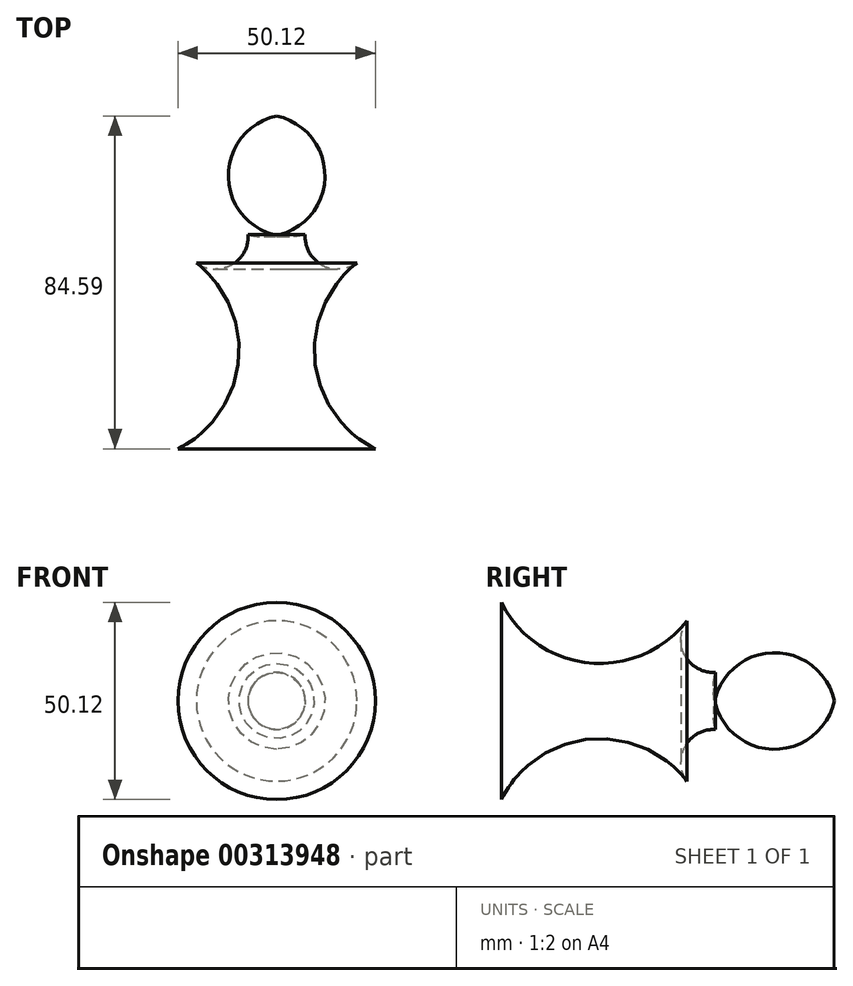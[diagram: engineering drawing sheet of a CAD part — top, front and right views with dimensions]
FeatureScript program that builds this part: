
annotation { "Feature Type Name" : "Feature", "Feature Type Description" : "" }
export const myFeature = defineFeature(function(context is Context, id is Id, definition is map)
    precondition{}
    {
        {
            var Q0;
            Q0=qCreatedBy(makeId("Top.planeOp"),FACE);
            var sketch = newSketch(context, id + "F0", { "sketchPlane" : qUnion([Q0])});
            skLineSegment(sketch, "E0", {"start": v(0, 44.58) * mm, "end": v(0, -40) * mm});
            skArc(sketch, "E1", {"start": v(0, 14.22) * mm, "mid": v(18.78, 29.4) * mm, "end": v(0, 44.58) * mm});
            skArc(sketch, "E2", {"start": v(7.25, 14.4) * mm, "mid": v(11.73, 6.55) * mm, "end": v(20.73, 7.47) * mm});
            skLineSegment(sketch, "E3", {"start": v(0, -40) * mm, "end": v(25.06, -40) * mm});
            skArc(sketch, "E4", {"start": v(20.73, 7.47) * mm, "mid": v(9.67, -17.48) * mm, "end": v(25.06, -40) * mm});
            skSolve(sketch);
        }
        {
            var Q0;
            {var subQ7=sQuery(id+"F0.wireOp",EDGE,"E3");Q0=makeQuery(id+"F0.imprint","IMPRINT",FACE,{"disambiguationData":[TD([[makeQuery(id+"F0.imprint","IMPRINT",EDGE,{"derivedFrom":subQ7}),1.0]])]});}
            var Q1;
            {var subQ0=sQuery(id+"F0.wireOp",EDGE,"E1");var subQ1=sQuery(id+"F0.wireOp",EDGE,"E0");var subQ2=makeQuery(id+"F0.imprint","INTERSECT",VERTEX,{"disambiguationData":[OD(0.0)],"derivedFrom":[subQ1,subQ0]});Q1=makeQuery(id+"F0.imprint","IMPRINT",FACE,{"disambiguationData":[TD([[makeQuery(id+"F0.imprint","IMPRINT",EDGE,{"disambiguationData":[TD([[subQ2,-1.0]])],"derivedFrom":subQ1}),1.0]])]});}
            var Q2;
            Q2=sQuery(id+"F0.wireOp",EDGE,"E0");
            revolve(context, id + "F1", {"entities" : qUnion([Q0, Q1]), "axis" : qUnion([Q2]), "revolveType" : RevolveType.FULL});
        }
    });
